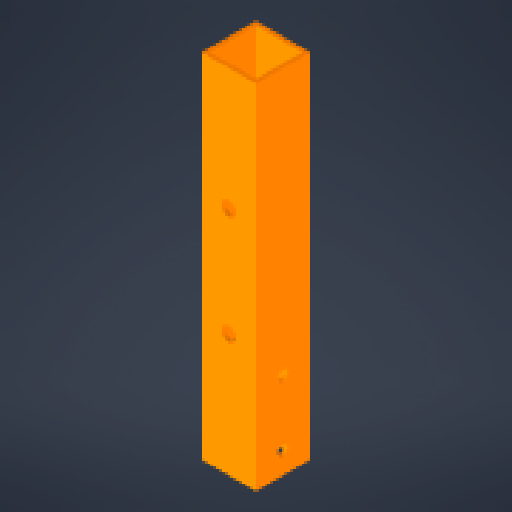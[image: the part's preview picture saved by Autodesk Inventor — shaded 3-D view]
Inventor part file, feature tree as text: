
AUTODESK INVENTOR PART (.ipt)
format: ipt  version: 2024 (Build 280153000, 153)  size: 164,352 bytes
history: native  units: mm
features: other x5, reference x4, extrude x3, sketch x3
ambient origin geometry x8: Origin, YZ Plane, XZ Plane, XY Plane, X Axis, Y Axis, Z Axis, Center Point
bodies: Body1 (feature_tree)
feature tree (15):
  other  "Твердое тело1"
  extrude  "Выдавливание1"  Depth=20.0mm
  extrude  "Выдавливание2"  Depth=1.5mm
  extrude  "Выдавливание3"  Depth=130.0mm TaperAngle=0.0deg
  sketch  "Эскиз1"
  sketch  "Эскиз2"
  sketch  "Эскиз3"
  reference  "Ссылка1"
  reference  "Ссылка2"
  reference  "Ссылка3"
  reference  "Ссылка4"
  parser-record x1  (decoder bookkeeping rows leaked as tree rows — omitted from the tree; the rows remain in map.json)
  other  "base_assambly.iam"
  other  "fb_axis:1"
  other  "fb_axis:2"
note: 1 file-system path scrubbed to <path> (originals preserved in map.json)
